# Revit family: Reduziermuffe
name_source: partatom
category: HLS-Bauteile
revit_build: Autodesk Revit 2017 (Build: 20190507_1515(x64)
units: mm (PartAtom-declared; Revit-internal decimal feet)

## family parameters
Arbeitsebenenbasiert = Nein
Beim Laden mit Abzugskörper schneiden = Nein
Bemaßung runder Anschluss = Durchmesser verwenden
Gemeinsam genutzt = Ja
Immer vertikal = Nein
Raumberechnungspunkt = Nein
Teiletyp = Normal

## types (5) — shared parameters
Firma = MEFA Befestigungs- und Montagesysteme GmbH
L1 = 23 mm  [stored 0.0754593 ft]
L2 = 17 mm
Länge = 40 mm  [stored 0.131234 ft]

## per-type parameters (varying)
| type | Artikelnummer | D | D0 | EAN | Fabrikat | Gewicht | Gewicht pro Bauteil | Innengewinde 1 | Innengewinde 2 | Kurztext1 | Kurztext2 | Länge Innengewinde 1 | Länge Innengewinde 2 | Material | Mengeneinheit | Oberflaeche | d1 | vpe |
| Reduziermuffe M 8-M10 | 0710016 | 16 mm  [stored 0.0524934 ft] | 11 mm  [stored 0.0360892 ft] | 4250928416315 | MEFA | 0.05 kg | 0.05 kg | M8 | M10 | Reduziermuffe rund | Innengew. M8 auf Innengew. M10 L= 40 mm | 16 mm | 20 mm | Stahl | St | galvanisch verzinkt | 7 mm  [stored 0.0229659 ft] | 100 St |
| Reduziermuffe M 8-M12 | 0710024 | 16 mm  [stored 0.0524934 ft] | 13 mm | 4250928416322 | MEFA | 0.04 kg | 0.04 kg | M8 | M12 | Reduziermuffe rund | Innengew. M8 auf Innengew. M12 L= 40 mm | 16 mm | 20 mm | Stahl | St | galvanisch verzinkt | 7 mm  [stored 0.0229659 ft] | 100 St |
| Reduziermuffe M10-M12 | 0710032 | 16 mm  [stored 0.0524934 ft] | 13 mm | 4250928416339 | MEFA | 0.04 kg | 0.04 kg | M10 | M12 | Reduziermuffe rund | Innengew. M10 auf Innengew. M12 L= 40 mm | 16 mm | 20 mm | Stahl | St | galvanisch verzinkt | 11 mm  [stored 0.0360892 ft] | 100 St |
| Reduziermuffe M10-M14 |  | 22 mm  [stored 0.0721785 ft] | 15 mm |  |  | 0.00 kg | 0.00 kg |  |  |  |  |  |  |  |  |  | 11 mm  [stored 0.0360892 ft] |  |
| Reduziermuffe M12-M16 | 0710105 | 22 mm  [stored 0.0721785 ft] | 17 mm | 4250928416346 | MEFA | 0.08 kg | 0.08 kg | M12 | M16 | Reduziermuffe rund | Innengew. M12 auf Innengew. M16 L= 40 mm | 16 mm | 20 mm | Stahl | St | galvanisch verzinkt | 13 mm | 25 St |

note: [stored X ft] marks values corroborated as IEEE doubles in the binary element streams (Revit-internal decimal feet)
